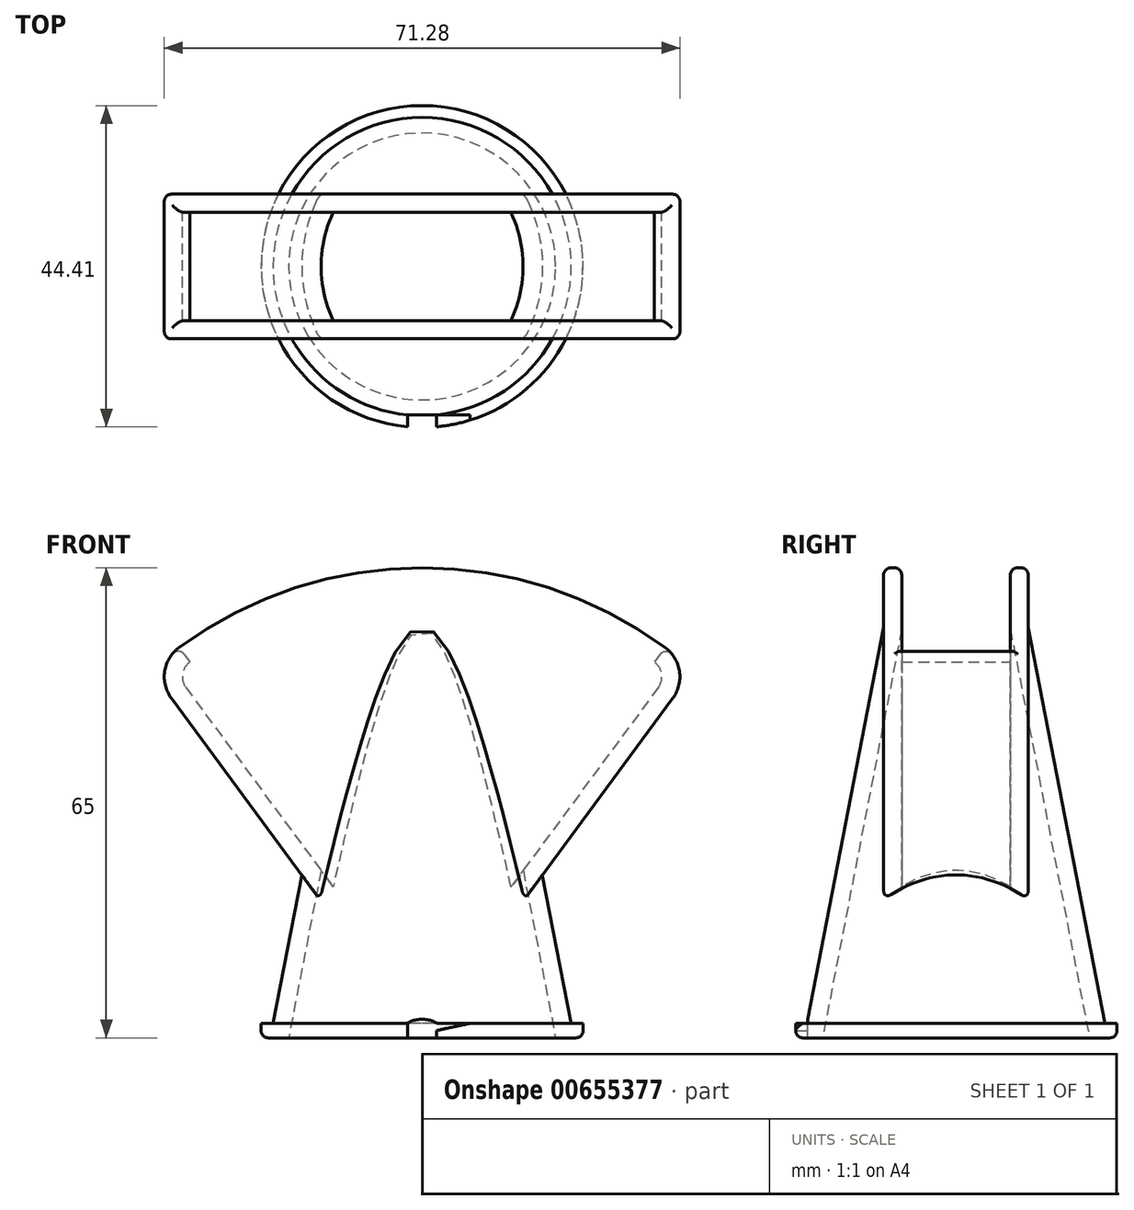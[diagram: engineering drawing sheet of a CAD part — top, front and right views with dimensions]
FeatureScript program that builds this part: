
annotation { "Feature Type Name" : "Feature", "Feature Type Description" : "" }
export const myFeature = defineFeature(function(context is Context, id is Id, definition is map)
    precondition{}
    {
        {
            var Q0;
            Q0=qCreatedBy(makeId("Top.planeOp"),FACE);
            var sketch = newSketch(context, id + "F0", { "sketchPlane" : qUnion([Q0])});
            skCircle(sketch, "E0", {"center": v(0, 0) * mm, "radius": 22.25 * mm});
            skSolve(sketch);
        }
        {
            var Q0;
            Q0=makeQuery(id+"F0.imprint","IMPRINT",FACE,{"disambiguationData":[TD([[makeQuery(id+"F0.imprint","IMPRINT",EDGE,{"derivedFrom":sQuery(id+"F0.wireOp",EDGE,"E0")}),1.0]])]});
            extrude(context, id + "F1", {"entities" : qUnion([Q0]), "depth" : 2 * mm, "offsetDistance" : 25 * mm});
        }
        {
            var Q0;
            Q0=qCreatedBy(makeId("Front.planeOp"),FACE);
            var sketch = newSketch(context, id + "F2", { "sketchPlane" : qUnion([Q0])});
            skLineSegment(sketch, "E1", {"start": v(0, 0) * mm, "end": v(21, 0) * mm});
            skLineSegment(sketch, "E2", {"start": v(21, 0) * mm, "end": v(10, 56.77) * mm});
            skLineSegment(sketch, "E3", {"start": v(10, 56.77) * mm, "end": v(0, 56.77) * mm});
            skLineSegment(sketch, "E4", {"start": v(0, 56.77) * mm, "end": v(0, 0) * mm});
            skSolve(sketch);
        }
        {
            var Q0;
            Q0=makeQuery(id+"F2.imprint","IMPRINT",FACE,{"disambiguationData":[TD([[makeQuery(id+"F2.imprint","IMPRINT",EDGE,{"derivedFrom":sQuery(id+"F2.wireOp",EDGE,"E1")}),1.0]])]});
            var Q1;
            Q1=sQuery(id+"F2.wireOp",EDGE,"E4");
            revolve(context, id + "F3", {"operationType" : NewBodyOperationType.ADD, "entities" : qUnion([Q0]), "axis" : qUnion([Q1]), "revolveType" : RevolveType.FULL});
        }
        {
            var Q0;
            Q0=qCreatedBy(makeId("Front.planeOp"),FACE);
            var sketch = newSketch(context, id + "F4", { "sketchPlane" : qUnion([Q0])});
            skLineSegment(sketch, "E5", {"start": v(0, 0) * mm, "end": v(0, 65) * mm, "construction": true});
            skLineSegment(sketch, "E6", {"start": v(34.66, 46.98) * mm, "end": v(0, 0) * mm});
            skLineSegment(sketch, "E7.MirrorCS", {"start": v(-34.66, 46.98) * mm, "end": v(0, 0) * mm});
            skLineSegment(sketch, "E8", {"start": v(0, 65) * mm, "end": v(0, 55) * mm, "construction": true});
            skLineSegment(sketch, "E9", {"start": v(0, 55) * mm, "end": v(37.5, 50.83) * mm, "construction": true});
            skLineSegment(sketch, "E10", {"start": v(37.5, 50.83) * mm, "end": v(-37.5, 50.83) * mm, "construction": true});
            skArc(sketch, "E11", {"start": v(33.6, 53.97) * mm, "mid": v(0, 65) * mm, "end": v(-33.6, 53.97) * mm});
            skPoint(sketch, "E12.orphan", {"position": v(44.38, 60.15) * mm});
            skPoint(sketch, "E13.MirrorCS.end.orphan", {"position": v(-44.38, 60.15) * mm});
            skPoint(sketch, "E13.MirrorCS.start.orphan", {"position": v(0, 65) * mm});
            skPoint(sketch, "E14.visualSharp", {"position": v(37.5, 50.83) * mm});
            skArc(sketch, "E14.filletArc", {"start": v(34.66, 46.98) * mm, "mid": v(35.58, 50.7) * mm, "end": v(33.6, 53.97) * mm});
            skPoint(sketch, "E15.visualSharp", {"position": v(-37.5, 50.83) * mm});
            skArc(sketch, "E15.filletArc", {"start": v(-33.6, 53.97) * mm, "mid": v(-35.58, 50.7) * mm, "end": v(-34.66, 46.98) * mm});
            skSolve(sketch);
        }
        {
            var Q0;
            Q0=makeQuery(id+"F4.imprint","IMPRINT",FACE,{"disambiguationData":[TD([[makeQuery(id+"F4.imprint","IMPRINT",EDGE,{"derivedFrom":sQuery(id+"F4.wireOp",EDGE,"E6")}),-1.0]])]});
            extrude(context, id + "F5", {"entities" : qUnion([Q0]), "operationType" : NewBodyOperationType.ADD, "depth" : 20 * mm, "offsetDistance" : 25 * mm, "symmetric" : true});
        }
        {
            var Q0;
            Q0=makeQuery(id+"F5.opExtrude","SWEPT_FACE",FACE,{"disambiguationData":[OSD([sQuery(id+"F4.wireOp",EDGE,"E11")])]});
            var Q1;
            Q1=makeQuery(id+"F1.opExtrude","CAP_FACE",FACE,{"disambiguationData":[OSD([sQuery(id+"F0.wireOp",EDGE,"E0")])],"isStart":true});
            shell(context, id + "F6", {"entities" : qUnion([Q0, Q1]), "thickness" : 2.5 * mm});
        }
        {
            var Q0;
            Q0=makeQuery(id+"F5.opExtrude","CAP_EDGE",EDGE,{"disambiguationData":[OSD([sQuery(id+"F4.wireOp",EDGE,"E14.filletArc")])],"isStart":true});
            fillet(context, id + "F7", {"entities" : qUnion([Q0]), "radius" : 1 * mm, "tangentPropagation" : true, "allowEdgeOverflow" : false});
        }
        {
            var Q0;
            Q0=makeQuery(id+"F5.opExtrude","CAP_EDGE",EDGE,{"disambiguationData":[OSD([sQuery(id+"F4.wireOp",EDGE,"E11")])],"isStart":false});
            var Q1;
            Q1=makeQuery(id+"F5.opExtrude","CAP_EDGE",EDGE,{"disambiguationData":[OSD([sQuery(id+"F4.wireOp",EDGE,"E15.filletArc")])],"isStart":false});
            var Q2;
            Q2=makeQuery(id+"F5.opExtrude","CAP_EDGE",EDGE,{"disambiguationData":[OSD([sQuery(id+"F4.wireOp",EDGE,"E14.filletArc")])],"isStart":false});
            fillet(context, id + "F8", {"entities" : qUnion([Q0, Q1, Q2]), "radius" : 1 * mm, "tangentPropagation" : true, "allowEdgeOverflow" : false});
        }
        {
            var Q0;
            Q0=makeQuery(id+"F6.opShell","OFFSET_EDGE",EDGE,{"disambiguationData":[OSD([sQuery(id+"F4.wireOp",EDGE,"E11"),sQuery(id+"F4.wireOp",EDGE,"E15.filletArc")]),OD(1.0)]});
            var Q1;
            Q1=makeQuery(id+"F6.opShell","OFFSET_EDGE",EDGE,{"disambiguationData":[OSD([sQuery(id+"F4.wireOp",EDGE,"E11"),sQuery(id+"F4.wireOp",EDGE,"E14.filletArc")]),OD(1.0)]});
            var Q2;
            {var subQ0=sQuery(id+"F4.wireOp",EDGE,"E11");Q2=makeQuery(id+"F6.opShell","OFFSET_EDGE",EDGE,{"disambiguationData":[OSD([subQ0]),TDD([makeQuery(id+"F5.opExtrude","CAP_EDGE",EDGE,{"disambiguationData":[OSD([subQ0])],"isStart":true})])]});}
            var Q3;
            {var subQ0=sQuery(id+"F4.wireOp",EDGE,"E11");Q3=makeQuery(id+"F6.opShell","OFFSET_EDGE",EDGE,{"disambiguationData":[OSD([subQ0]),TDD([makeQuery(id+"F5.opExtrude","CAP_EDGE",EDGE,{"disambiguationData":[OSD([subQ0])],"isStart":false})])]});}
            fillet(context, id + "F9", {"entities" : qUnion([Q0, Q1, Q2, Q3]), "radius" : 1 * mm, "tangentPropagation" : true, "allowEdgeOverflow" : false});
        }
        {
            var Q0;
            Q0=makeQuery(id+"F1.opExtrude","CAP_EDGE",EDGE,{"disambiguationData":[OSD([sQuery(id+"F0.wireOp",EDGE,"E0")])],"isStart":true});
            fillet(context, id + "F10", {"entities" : qUnion([Q0]), "radius" : 1 * mm, "tangentPropagation" : true, "allowEdgeOverflow" : false});
        }
        {
            var Q0;
            Q0=qCreatedBy(makeId("Front.planeOp"),FACE);
            var sketch = newSketch(context, id + "F11", { "sketchPlane" : qUnion([Q0])});
            skLineSegment(sketch, "E16", {"start": v(0, 0) * mm, "end": v(2, 0) * mm, "construction": true});
            skLineSegment(sketch, "E17", {"start": v(2, 0) * mm, "end": v(-2, 0) * mm, "construction": true});
            skLineSegment(sketch, "E18.bottom", {"start": v(-2, 0) * mm, "end": v(2, 0) * mm});
            skLineSegment(sketch, "E18.top", {"start": v(-2, 4) * mm, "end": v(2, 4) * mm});
            skLineSegment(sketch, "E18.left", {"start": v(-2, 0) * mm, "end": v(-2, 4) * mm});
            skLineSegment(sketch, "E18.right", {"start": v(2, 0) * mm, "end": v(2, 4) * mm});
            skLineSegment(sketch, "E19", {"start": v(2, 1.02) * mm, "end": v(7.54, 2.19) * mm});
            skLineSegment(sketch, "E20", {"start": v(7.54, 2.19) * mm, "end": v(2, 2.19) * mm});
            skLineSegment(sketch, "E21", {"start": v(2, 2.19) * mm, "end": v(2, 1.02) * mm});
            skSolve(sketch);
        }
        {
            var Q0;
            Q0 = qSketchRegion(id + "F11", true);
            extrude(context, id + "F12", {"entities" : qUnion([Q0]), "operationType" : NewBodyOperationType.REMOVE, "depth" : 22.5 * mm, "offsetDistance" : 25 * mm, "hasSecondDirection" : true, "secondDirectionOppositeDirection" : false, "secondDirectionDepth" : 20.5 * mm});
        }
    });
